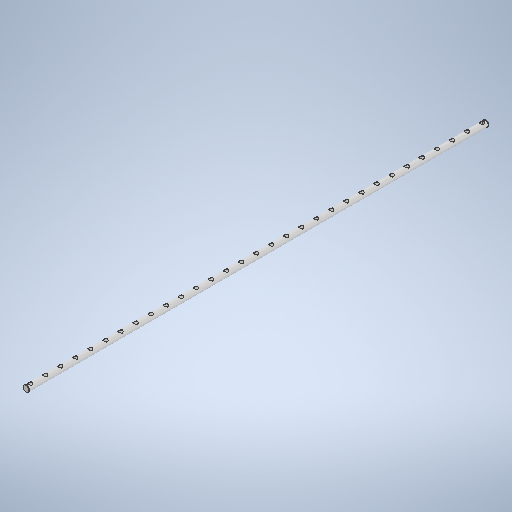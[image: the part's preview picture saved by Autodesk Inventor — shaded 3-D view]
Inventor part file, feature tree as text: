
AUTODESK INVENTOR PART (.ipt)
format: ipt  version: 2025.3 (Build 293356000, 356)  size: 394,752 bytes
history: native  units: mm
features: sketch x5, extrude x4, other x1
ambient origin geometry x8: Origin, YZ Plane, XZ Plane, XY Plane, X Axis, Y Axis, Z Axis, Center Point
bodies: Body1 (feature_tree)
feature tree (10):
  other  "Sólido1"
  extrude  "Extrusión1"  Depth=68.0mm
  extrude  "Extrusión2"  Depth=79.0mm
  extrude  "Extrusión3"  Depth=5.0mm TaperAngle=0.0deg
  extrude  "Extrusión4"  Depth=10.0mm
  sketch  "Boceto1"  dims[d0=76.2mm d1=68.0mm]
  sketch  "Boceto2"  dims[d5=5.0mm d6=5.0mm d7=0.0mm d8=0.0mm d9=5.0mm d10=5.0mm d11=0.0mm d12=0.0mm]
  sketch  "Boceto3"  dims[d13=50.0mm d14=310.0mm d16=200.0mm d17=10.0mm d19=10.0mm]
  sketch  "Boceto4"  dims[d21=50.0mm d22=0.0mm]
  sketch  "Boceto - Patrón rectangular1"  dims[d2=6100.0mm d3=0.0mm d4=79.0mm]
